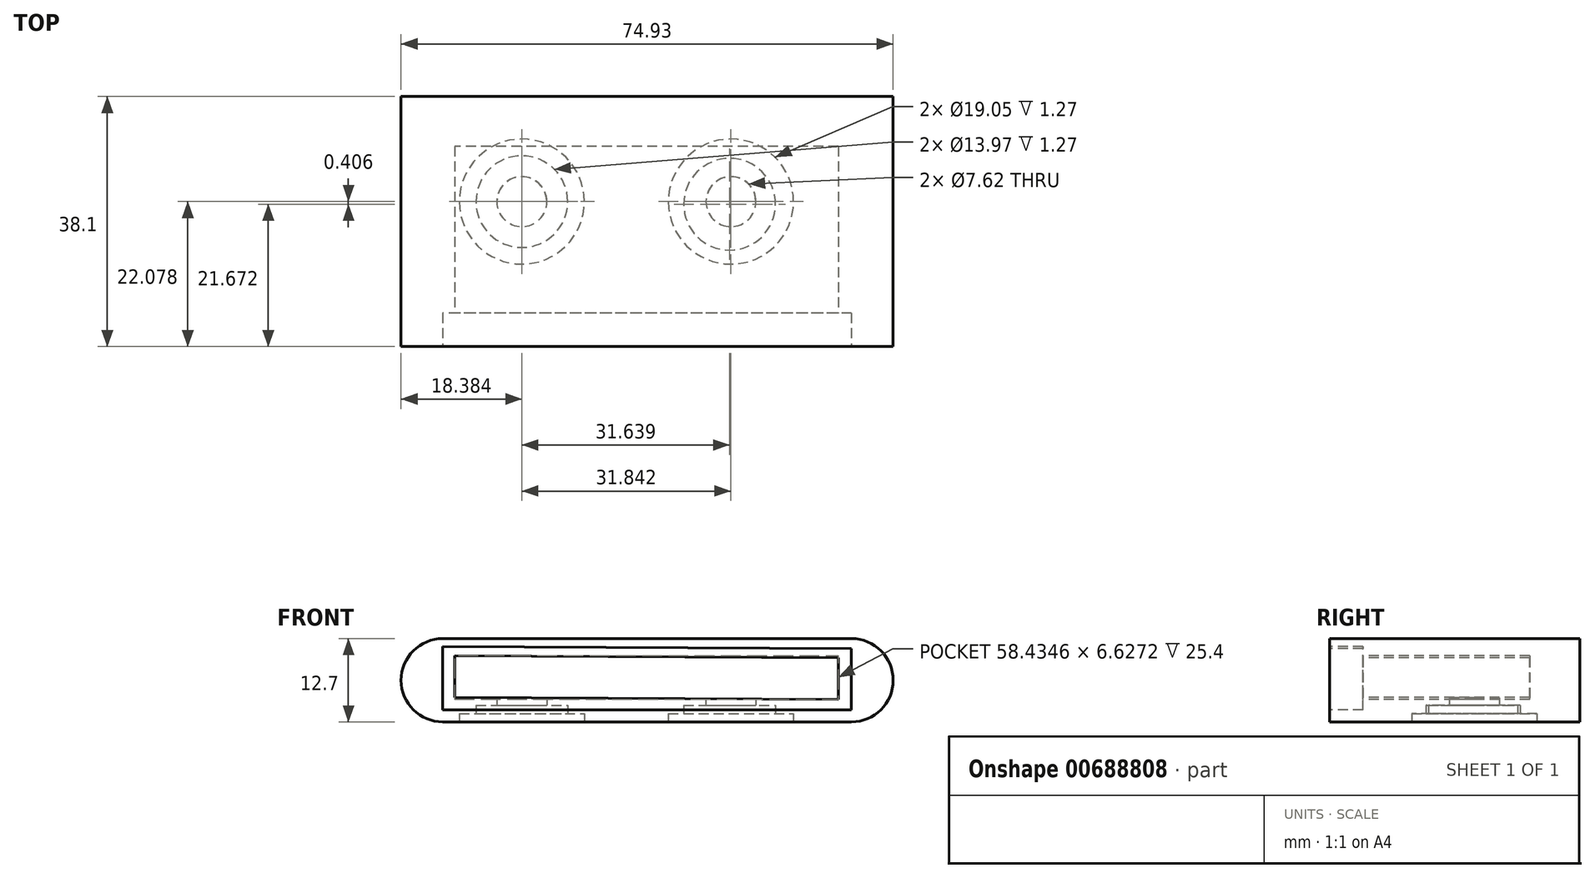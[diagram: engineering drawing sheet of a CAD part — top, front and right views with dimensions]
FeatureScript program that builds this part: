
annotation { "Feature Type Name" : "Feature", "Feature Type Description" : "" }
export const myFeature = defineFeature(function(context is Context, id is Id, definition is map)
    precondition{}
    {
        {
            var Q0;
            Q0=qCreatedBy(makeId("Front.planeOp"),FACE);
            var sketch = newSketch(context, id + "F0", { "sketchPlane" : qUnion([Q0])});
            skLineSegment(sketch, "E0", {"start": v(0, 0) * mm, "end": v(-62.23, 0) * mm});
            skLineSegment(sketch, "E1", {"start": v(0, 12.7) * mm, "end": v(0, 0) * mm});
            skLineSegment(sketch, "E2", {"start": v(-62.23, 0) * mm, "end": v(-62.23, 12.7) * mm});
            skLineSegment(sketch, "E3", {"start": v(-62.23, 12.7) * mm, "end": v(0, 12.7) * mm});
            skArc(sketch, "E4", {"start": v(-62.23, 12.7) * mm, "mid": v(-68.58, 6.35) * mm, "end": v(-62.23, 0) * mm});
            skArc(sketch, "E5", {"start": v(0, 0) * mm, "mid": v(6.35, 6.35) * mm, "end": v(0, 12.7) * mm});
            skSolve(sketch);
        }
        {
            var Q0;
            Q0 = qSketchRegion(id + "F0", true);
            extrude(context, id + "F1", {"entities" : qUnion([Q0]), "depth" : 38.1 * mm, "offsetDistance" : 25.4 * mm});
        }
        {
            var Q0;
            Q0=makeQuery(id+"F1.opExtrude","CAP_FACE",FACE,{"disambiguationData":[OSD([sQuery(id+"F0.wireOp",EDGE,"E0"),sQuery(id+"F0.wireOp",EDGE,"E3"),sQuery(id+"F0.wireOp",EDGE,"E4"),sQuery(id+"F0.wireOp",EDGE,"E5")])],"isStart":false});
            var sketch = newSketch(context, id + "F2", { "sketchPlane" : qUnion([Q0])});
            skLineSegment(sketch, "E6", {"start": v(0, 1.81) * mm, "end": v(0, 11.17) * mm});
            skLineSegment(sketch, "E7", {"start": v(0, 1.81) * mm, "end": v(-62.23, 1.81) * mm});
            skLineSegment(sketch, "E8", {"start": v(-62.23, 1.81) * mm, "end": v(-62.23, 11.47) * mm});
            skLineSegment(sketch, "E9", {"start": v(-62.23, 11.47) * mm, "end": v(0, 11.17) * mm});
            skSolve(sketch);
        }
        {
            var Q0;
            Q0 = qSketchRegion(id + "F2", true);
            extrude(context, id + "F3", {"entities" : qUnion([Q0]), "operationType" : NewBodyOperationType.REMOVE, "oppositeDirection" : true, "depth" : 5.08 * mm, "offsetDistance" : 25.4 * mm});
        }
        {
            var Q0;
            Q0=makeQuery(id+"F3.boolean.opBoolean","COPY",FACE,{"derivedFrom":makeQuery(id+"F3.opExtrude","CAP_FACE",FACE,{"disambiguationData":[OSD([sQuery(id+"F2.wireOp",EDGE,"E6"),sQuery(id+"F2.wireOp",EDGE,"E7"),sQuery(id+"F2.wireOp",EDGE,"E8"),sQuery(id+"F2.wireOp",EDGE,"E9")])],"isStart":false})});
            var sketch = newSketch(context, id + "F4", { "sketchPlane" : qUnion([Q0])});
            skLineSegment(sketch, "E10", {"start": v(-60.44, 3.72) * mm, "end": v(-60.44, 10.07) * mm});
            skLineSegment(sketch, "E11", {"start": v(-60.44, 10.07) * mm, "end": v(-2, 9.8) * mm});
            skLineSegment(sketch, "E12", {"start": v(-2, 9.8) * mm, "end": v(-2, 3.45) * mm});
            skLineSegment(sketch, "E13", {"start": v(-2, 3.45) * mm, "end": v(-60.44, 3.72) * mm});
            skSolve(sketch);
        }
        {
            var Q0;
            Q0 = qSketchRegion(id + "F4", true);
            extrude(context, id + "F5", {"entities" : qUnion([Q0]), "operationType" : NewBodyOperationType.REMOVE, "oppositeDirection" : true, "depth" : 25.4 * mm, "offsetDistance" : 25.4 * mm});
        }
        {
            var Q0;
            Q0=makeQuery(id+"F1.opExtrude","SWEPT_FACE",FACE,{"disambiguationData":[OSD([sQuery(id+"F0.wireOp",EDGE,"E0")])]});
            var sketch = newSketch(context, id + "F6", { "sketchPlane" : qUnion([Q0])});
            skCircle(sketch, "E14", {"center": v(-50.2, 16.02) * mm, "radius": 9.53 * mm});
            skCircle(sketch, "E15", {"center": v(-18.35, 16.02) * mm, "radius": 9.53 * mm});
            skSolve(sketch);
        }
        {
            var Q0;
            Q0 = qSketchRegion(id + "F6", true);
            extrude(context, id + "F7", {"entities" : qUnion([Q0]), "operationType" : NewBodyOperationType.REMOVE, "oppositeDirection" : true, "depth" : 1.27 * mm, "offsetDistance" : 25.4 * mm});
        }
        {
            var Q0;
            Q0=makeQuery(id+"F7.boolean.opBoolean","COPY",FACE,{"derivedFrom":makeQuery(id+"F7.opExtrude","CAP_FACE",FACE,{"disambiguationData":[OSD([sQuery(id+"F6.wireOp",EDGE,"E14")])],"isStart":false})});
            var sketch = newSketch(context, id + "F8", { "sketchPlane" : qUnion([Q0])});
            skCircle(sketch, "E16", {"center": v(-50.2, 16.02) * mm, "radius": 6.99 * mm});
            skCircle(sketch, "E17", {"center": v(-18.56, 16.43) * mm, "radius": 6.99 * mm});
            skSolve(sketch);
        }
        {
            var Q0;
            Q0 = qSketchRegion(id + "F8", true);
            extrude(context, id + "F9", {"entities" : qUnion([Q0]), "operationType" : NewBodyOperationType.REMOVE, "oppositeDirection" : true, "depth" : 1.27 * mm, "offsetDistance" : 25.4 * mm});
        }
        {
            var Q0;
            Q0=makeQuery(id+"F9.boolean.opBoolean","COPY",FACE,{"derivedFrom":makeQuery(id+"F9.opExtrude","CAP_FACE",FACE,{"disambiguationData":[OSD([sQuery(id+"F8.wireOp",EDGE,"E16")])],"isStart":false})});
            var sketch = newSketch(context, id + "F10", { "sketchPlane" : qUnion([Q0])});
            skCircle(sketch, "E18", {"center": v(-50.2, 16.02) * mm, "radius": 3.81 * mm});
            skCircle(sketch, "E19", {"center": v(-18.35, 16.02) * mm, "radius": 3.81 * mm});
            skSolve(sketch);
        }
        {
            var Q0;
            Q0 = qSketchRegion(id + "F10", true);
            extrude(context, id + "F11", {"entities" : qUnion([Q0]), "operationType" : NewBodyOperationType.REMOVE, "oppositeDirection" : true, "depth" : 1.27 * mm, "offsetDistance" : 25.4 * mm});
        }
    });
